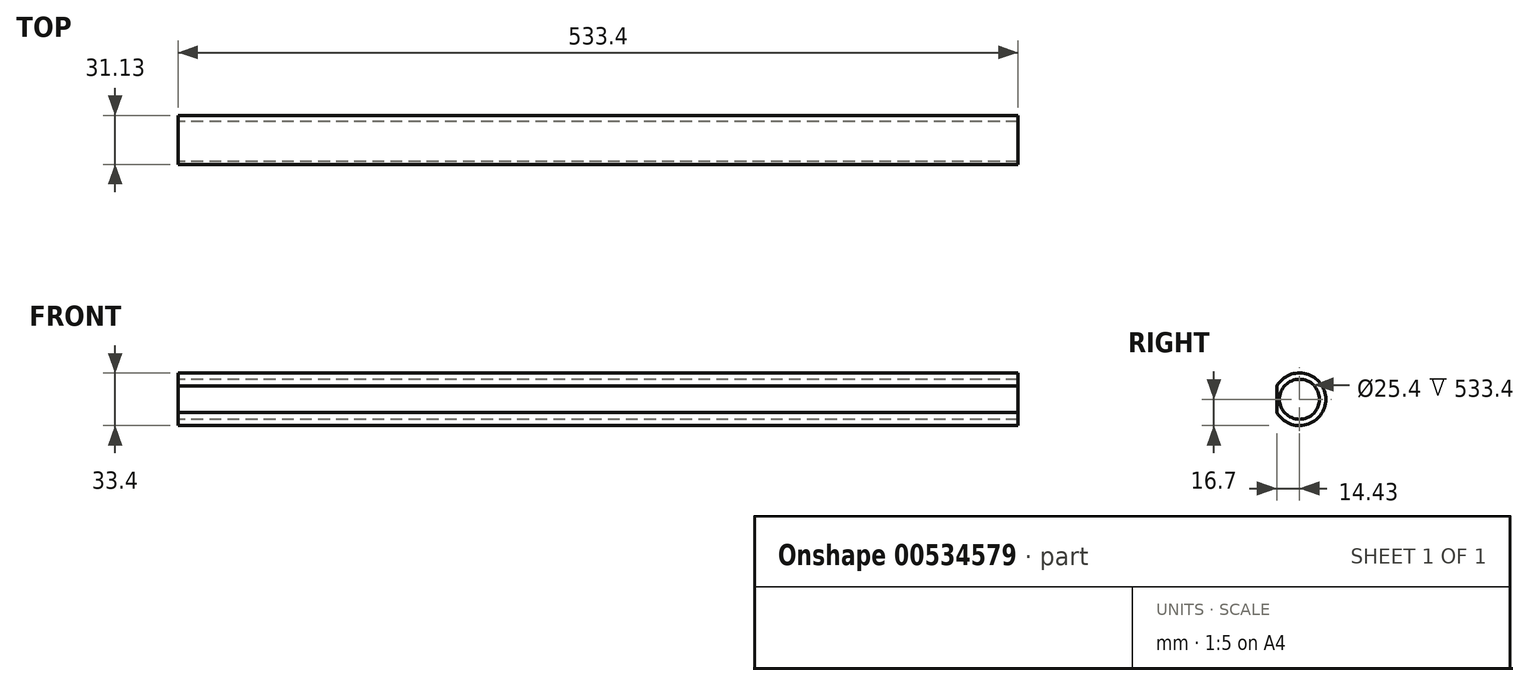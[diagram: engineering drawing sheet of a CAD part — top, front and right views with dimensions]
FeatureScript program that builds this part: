
annotation { "Feature Type Name" : "Feature", "Feature Type Description" : "" }
export const myFeature = defineFeature(function(context is Context, id is Id, definition is map)
    precondition{}
    {
        {
            var Q0;
            Q0=qCreatedBy(makeId("Right.planeOp"),FACE);
            var sketch = newSketch(context, id + "F0", { "sketchPlane" : qUnion([Q0])});
            skCircle(sketch, "E0", {"center": v(0, 0) * mm, "radius": 12.7 * mm});
            skCircle(sketch, "E1", {"center": v(0, 0) * mm, "radius": 16.7 * mm});
            skLineSegment(sketch, "E2", {"start": v(-14.43, -8.4) * mm, "end": v(-14.43, 8.4) * mm});
            skSolve(sketch);
        }
        {
            var Q0;
            {var subQ0=sQuery(id+"F0.wireOp",EDGE,"RQXjRciz-V3U8-3ciQ-oObN-kKmOUTi8DOiw");var subQ1=sQuery(id+"F0.wireOp",EDGE,"E0");var subQ2=makeQuery(id+"F0.imprint","INTERSECT",VERTEX,{"disambiguationData":[OD(0.0)],"derivedFrom":[subQ1,subQ0]});Q0=makeQuery(id+"F0.imprint","IMPRINT",FACE,{"disambiguationData":[TD([[makeQuery(id+"F0.imprint","IMPRINT",EDGE,{"disambiguationData":[TD([[subQ2,-1.0]])],"derivedFrom":subQ1}),-1.0]])]});}
            var Q1;
            Q1=makeQuery(id+"F0.imprint","IMPRINT",FACE,{"disambiguationData":[TD([[makeQuery(id+"F0.imprint","IMPRINT",EDGE,{"derivedFrom":sQuery(id+"F0.wireOp",EDGE,"E0")}),-1.0]])]});
            extrude(context, id + "F1", {"entities" : qUnion([Q0, Q1]), "depth" : 533.4 * mm, "offsetDistance" : 25.4 * mm});
        }
    });
